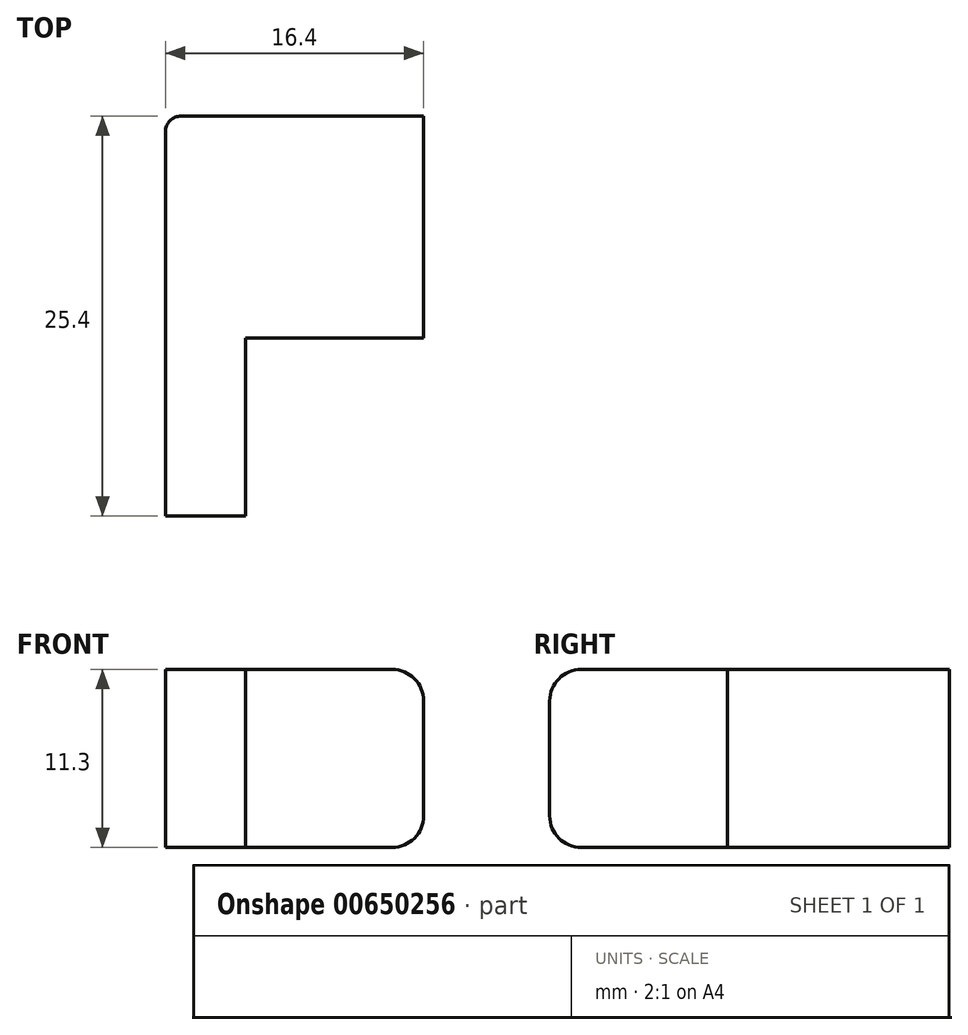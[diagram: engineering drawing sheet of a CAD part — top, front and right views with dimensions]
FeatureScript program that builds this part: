
annotation { "Feature Type Name" : "Feature", "Feature Type Description" : "" }
export const myFeature = defineFeature(function(context is Context, id is Id, definition is map)
    precondition{}
    {
        {
            var Q0;
            Q0=qCreatedBy(makeId("Top.planeOp"),FACE);
            var sketch = newSketch(context, id + "F0", { "sketchPlane" : qUnion([Q0])});
            skLineSegment(sketch, "E0.bottom", {"start": v(0, 0) * mm, "end": v(16.4, 0) * mm});
            skLineSegment(sketch, "E0.top", {"start": v(0, 25.4) * mm, "end": v(16.4, 25.4) * mm});
            skLineSegment(sketch, "E0.left", {"start": v(0, 0) * mm, "end": v(0, 25.4) * mm});
            skLineSegment(sketch, "E0.right", {"start": v(16.4, 0) * mm, "end": v(16.4, 25.4) * mm});
            skSolve(sketch);
        }
        {
            var Q0;
            Q0=makeQuery(id+"F0.imprint","IMPRINT",FACE,{"disambiguationData":[TD([[makeQuery(id+"F0.imprint","IMPRINT",EDGE,{"derivedFrom":sQuery(id+"F0.wireOp",EDGE,"E0.bottom")}),1.0]])]});
            extrude(context, id + "F1", {"entities" : qUnion([Q0]), "depth" : 11.3 * mm, "offsetDistance" : 25 * mm});
        }
        {
            var Q0;
            Q0=makeQuery(id+"F1.opExtrude","CAP_FACE",FACE,{"disambiguationData":[OSD([sQuery(id+"F0.wireOp",EDGE,"E0.bottom"),sQuery(id+"F0.wireOp",EDGE,"E0.top"),sQuery(id+"F0.wireOp",EDGE,"E0.left"),sQuery(id+"F0.wireOp",EDGE,"E0.right")])],"isStart":false});
            var sketch = newSketch(context, id + "F2", { "sketchPlane" : qUnion([Q0])});
            skLineSegment(sketch, "E1.bottom", {"start": v(16.4, 0) * mm, "end": v(5.1, 0) * mm});
            skLineSegment(sketch, "E1.top", {"start": v(16.4, 11.3) * mm, "end": v(5.1, 11.3) * mm});
            skLineSegment(sketch, "E1.left", {"start": v(16.4, 0) * mm, "end": v(16.4, 11.3) * mm});
            skLineSegment(sketch, "E1.right", {"start": v(5.1, 0) * mm, "end": v(5.1, 11.3) * mm});
            skSolve(sketch);
        }
        {
            var Q0;
            Q0=makeQuery(id+"F2.imprint","IMPRINT",FACE,{"disambiguationData":[TD([[makeQuery(id+"F2.imprint","IMPRINT",EDGE,{"derivedFrom":sQuery(id+"F2.wireOp",EDGE,"E1.bottom")}),1.0]])]});
            extrude(context, id + "F3", {"entities" : qUnion([Q0]), "operationType" : NewBodyOperationType.REMOVE, "oppositeDirection" : true, "depth" : 25 * mm, "offsetDistance" : 25 * mm});
        }
        {
            var Q0;
            Q0=makeQuery(id+"F1.opExtrude","CAP_EDGE",EDGE,{"disambiguationData":[OSD([sQuery(id+"F0.wireOp",EDGE,"E0.right")])],"isStart":true});
            var Q1;
            Q1=makeQuery(id+"F1.opExtrude","CAP_EDGE",EDGE,{"disambiguationData":[OSD([sQuery(id+"F0.wireOp",EDGE,"E0.bottom")])],"isStart":true});
            var Q2;
            Q2=makeQuery(id+"F1.opExtrude","CAP_EDGE",EDGE,{"disambiguationData":[OSD([sQuery(id+"F0.wireOp",EDGE,"E0.bottom")])],"isStart":false});
            var Q3;
            Q3=makeQuery(id+"F1.opExtrude","CAP_EDGE",EDGE,{"disambiguationData":[OSD([sQuery(id+"F0.wireOp",EDGE,"E0.right")])],"isStart":false});
            fillet(context, id + "F4", {"entities" : qUnion([Q0, Q1, Q2, Q3]), "radius" : 2 * mm, "tangentPropagation" : true, "allowEdgeOverflow" : false});
        }
        {
            var Q0;
            Q0=makeQuery(id+"F1.opExtrude","SWEPT_EDGE",EDGE,{"disambiguationData":[OSD([sQuery(id+"F0.wireOp",EDGE,"E0.top"),sQuery(id+"F0.wireOp",EDGE,"E0.left")])]});
            fillet(context, id + "F5", {"entities" : qUnion([Q0]), "radius" : 1 * mm, "tangentPropagation" : true, "allowEdgeOverflow" : false});
        }
    });
